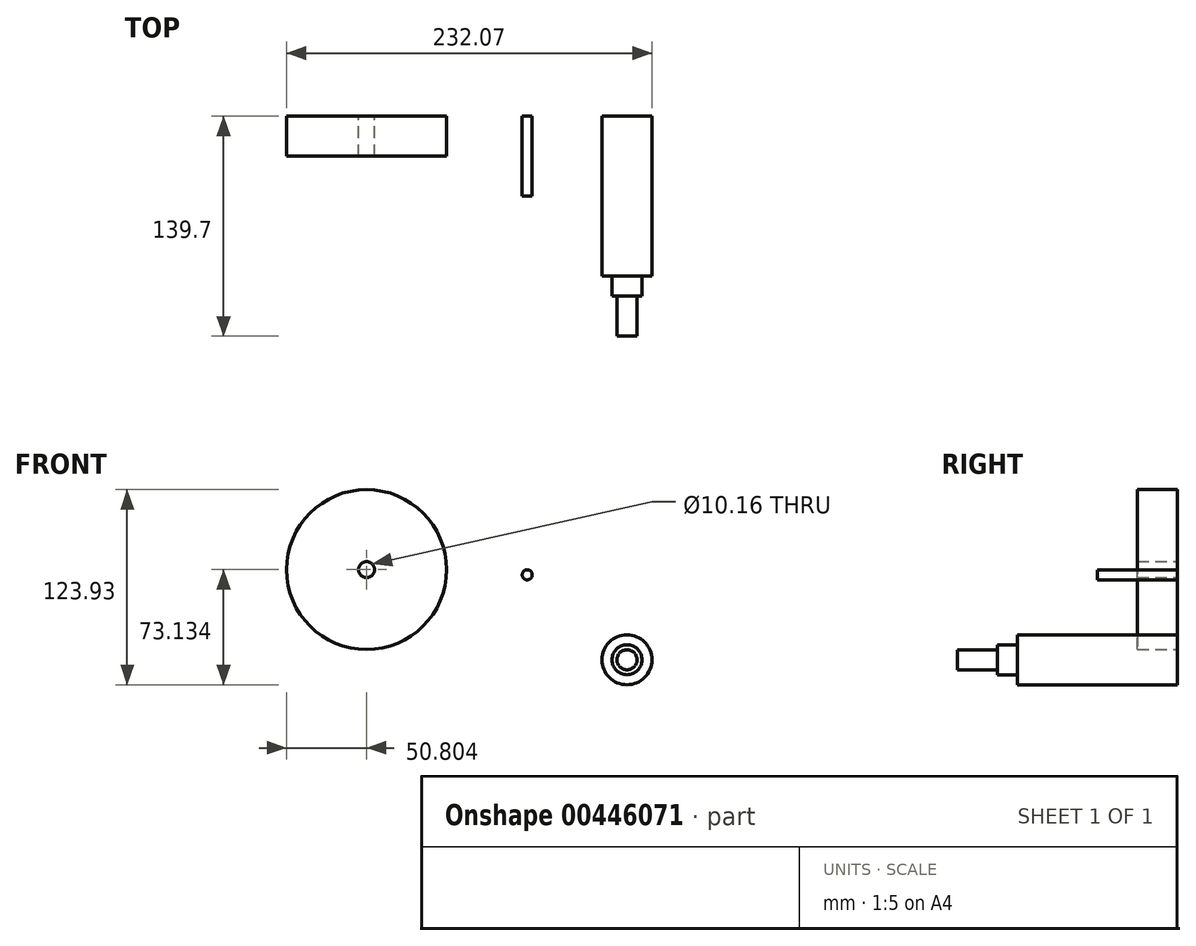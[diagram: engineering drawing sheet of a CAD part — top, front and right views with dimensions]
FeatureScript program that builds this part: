
annotation { "Feature Type Name" : "Feature", "Feature Type Description" : "" }
export const myFeature = defineFeature(function(context is Context, id is Id, definition is map)
    precondition{}
    {
        {
            var Q0;
            Q0=qCreatedBy(makeId("Front.planeOp"),FACE);
            var sketch = newSketch(context, id + "F0", { "sketchPlane" : qUnion([Q0])});
            skCircle(sketch, "E0", {"center": v(-39.54, 27.36) * mm, "radius": 3.2 * mm});
            skSolve(sketch);
        }
        {
            var Q0;
            Q0 = qSketchRegion(id + "F0", true);
            extrude(context, id + "F1", {"entities" : qUnion([Q0]), "depth" : 50.8 * mm});
        }
        {
            var Q0;
            Q0=qCreatedBy(makeId("Front.planeOp"),FACE);
            var sketch = newSketch(context, id + "F2", { "sketchPlane" : qUnion([Q0])});
            skCircle(sketch, "E1", {"center": v(-141.58, 30.68) * mm, "radius": 50.8 * mm});
            skCircle(sketch, "E2", {"center": v(-141.58, 30.68) * mm, "radius": 5.08 * mm});
            skSolve(sketch);
        }
        {
            var Q0;
            Q0=makeQuery(id+"F2.imprint","IMPRINT",FACE,{"disambiguationData":[TD([[makeQuery(id+"F2.imprint","IMPRINT",EDGE,{"derivedFrom":sQuery(id+"F2.wireOp",EDGE,"E1")}),1.0]])]});
            extrude(context, id + "F3", {"entities" : qUnion([Q0]), "depth" : 25.4 * mm});
        }
        {
            var Q0;
            Q0=qCreatedBy(makeId("Front.planeOp"),FACE);
            var sketch = newSketch(context, id + "F4", { "sketchPlane" : qUnion([Q0])});
            skCircle(sketch, "E3", {"center": v(23.81, -26.57) * mm, "radius": 15.88 * mm});
            skSolve(sketch);
        }
        {
            var Q0;
            Q0 = qSketchRegion(id + "F4", true);
            extrude(context, id + "F5", {"entities" : qUnion([Q0]), "depth" : 101.6 * mm});
        }
        {
            var Q0;
            Q0=makeQuery(id+"F5.opExtrude","CAP_FACE",FACE,{"disambiguationData":[OSD([sQuery(id+"F4.wireOp",EDGE,"E3")])],"isStart":false});
            var sketch = newSketch(context, id + "F6", { "sketchPlane" : qUnion([Q0])});
            skCircle(sketch, "E4", {"center": v(23.81, -26.57) * mm, "radius": 9.53 * mm});
            skSolve(sketch);
        }
        {
            var Q0;
            Q0=makeQuery(id+"F6.imprint","IMPRINT",FACE,{"disambiguationData":[TD([[makeQuery(id+"F6.imprint","IMPRINT",EDGE,{"derivedFrom":sQuery(id+"F6.wireOp",EDGE,"E4")}),1.0]])]});
            extrude(context, id + "F7", {"entities" : qUnion([Q0]), "operationType" : NewBodyOperationType.ADD, "depth" : 12.7 * mm});
        }
        {
            var Q0;
            Q0=makeQuery(id+"F7.opExtrude","CAP_FACE",FACE,{"disambiguationData":[OSD([sQuery(id+"F6.wireOp",EDGE,"E4")])],"isStart":false});
            var sketch = newSketch(context, id + "F8", { "sketchPlane" : qUnion([Q0])});
            skCircle(sketch, "E5", {"center": v(23.81, -26.57) * mm, "radius": 6.35 * mm});
            skSolve(sketch);
        }
        {
            var Q0;
            Q0 = qSketchRegion(id + "F8", true);
            extrude(context, id + "F9", {"entities" : qUnion([Q0]), "operationType" : NewBodyOperationType.ADD, "depth" : 25.4 * mm});
        }
    });
